# Revit family: Shower-Shower_Arm-KOHLER-Gooseneck-K-76336
name_source: partatom
category: Plumbing Fixtures
revit_build: Autodesk Revit 2017 (Build: 20160225_1515(x64)
units: mm (PartAtom-declared; Revit-internal decimal feet)

## family parameters
Cut with Voids When Loaded = No
Host = Face
OmniClass Number = 23.31.25.00
OmniClass Title = Toilet and Bath Specialties
Part Type = Normal
Room Calculation Point = No
Round Connector Dimension = Use Diameter
Shared = No

## types (5) — shared parameters
ADA Compliant = No
Assembly Code = D2010700
CW Connection = No
Cold Water Inlet = Cold Water Inlet
Date Modified = 12/16/2020
Default Elevation = 72"
Description = Rainhead arm with 3-way diverter
Drain Included = No
Flow Rate = 0 GPM
HW Connection = Yes
Height = 7 7/16"
Hot Water Inlet = Hot Water Inlet
Length = 18 3/16"
Manufacturer = KOHLER Co.
Master Format 2014 = 22 42 23
Master Format 2014 Name = Residential Showers
Material = Premium Metal Construction
Pressure = 0.00 psi
Product Documentation Link = https://www.us.kohler.com
Product Name = Gooseneck
Product Page URL = http://www.us.kohler.com
Tempered Water Inlet = Tempered Water Inlet
URL = https://www.us.kohler.com
Vent Connection = No
Waste Connection = No
Waste Water Outlet = Waste Water Outlet
WaterSense Certified = No
Width = 2 1/2"

## per-type parameters (varying)
| type | Finish | Model | Type |
| CP-Polished Chrome | Kohler-Metal-CP-Polished_Chrome | K-76336-CP | 1 |
| SN-Vibrant  Polished Nickel | Kohler-Metal-SN-Vibrant_Polished_Nickel | K-76336-SN | 2 |
| BN-Vibrant  Brushed Nicke | Kohler-Metal-BN-Vibrant_Brushed_Nickel | K-76336-BN | 3 |
| BV-Vibrant  Brushed Bronze | Kohler-Metal-BV-Brushed_Bronze | K-76336-BV | 4 |
| 2BZ-Oil Rubbed Bronze | Kohler-Metal-2BZ-Oil_Rubbed_Bronze | K-76336-2BZ | 5 |

## geometry (parser evidence)
native form markers: Sweep x5
no freeform markers — native parametric forms only
